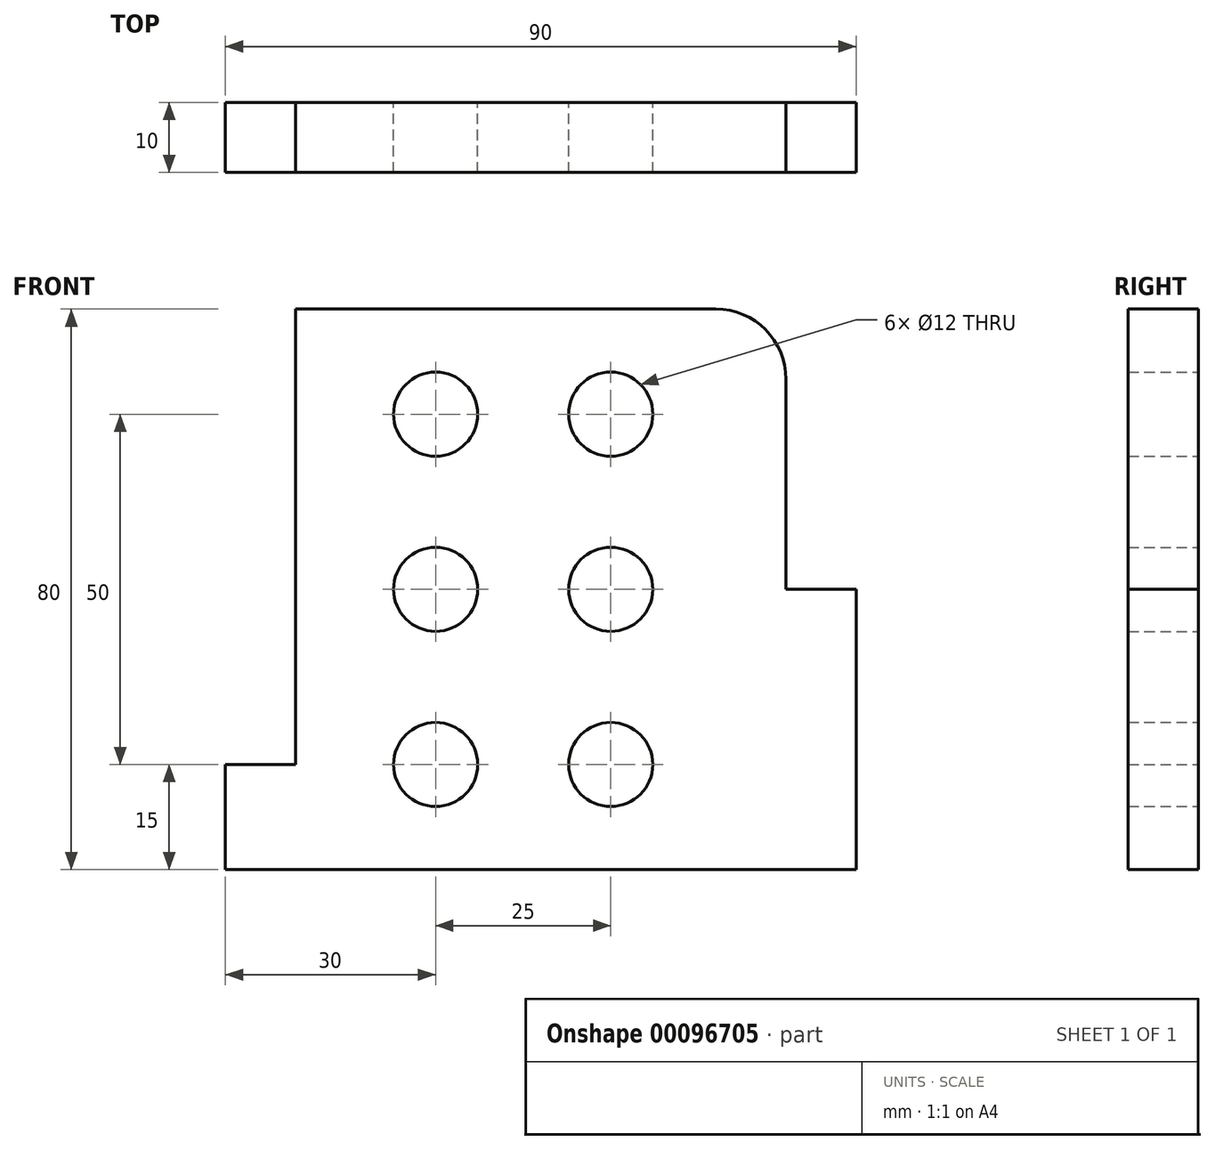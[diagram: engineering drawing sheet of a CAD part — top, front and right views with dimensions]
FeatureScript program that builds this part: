
annotation { "Feature Type Name" : "Feature", "Feature Type Description" : "" }
export const myFeature = defineFeature(function(context is Context, id is Id, definition is map)
    precondition{}
    {
        {
            var Q0;
            Q0=qCreatedBy(makeId("Front.planeOp"),FACE);
            var sketch = newSketch(context, id + "F0", { "sketchPlane" : qUnion([Q0])});
            skLineSegment(sketch, "E0", {"start": v(0, 0) * mm, "end": v(0, 15) * mm});
            skLineSegment(sketch, "E1", {"start": v(10, 15) * mm, "end": v(10, 80) * mm});
            skLineSegment(sketch, "E2", {"start": v(10, 80) * mm, "end": v(70, 80) * mm});
            skLineSegment(sketch, "E3", {"start": v(0, 0) * mm, "end": v(90, 0) * mm});
            skLineSegment(sketch, "E4", {"start": v(90, 0) * mm, "end": v(90, 40) * mm});
            skLineSegment(sketch, "E5", {"start": v(90, 40) * mm, "end": v(80, 40) * mm});
            skLineSegment(sketch, "E6", {"start": v(80, 40) * mm, "end": v(80, 70) * mm});
            skArc(sketch, "E7", {"start": v(80, 70) * mm, "mid": v(77.07, 77.07) * mm, "end": v(70, 80) * mm});
            skCircle(sketch, "E8", {"center": v(30, 15) * mm, "radius": 6 * mm});
            skCircle(sketch, "E9", {"center": v(55, 15) * mm, "radius": 6 * mm});
            skCircle(sketch, "E10", {"center": v(55, 40) * mm, "radius": 6 * mm});
            skCircle(sketch, "E11", {"center": v(30, 40) * mm, "radius": 6 * mm});
            skCircle(sketch, "E12", {"center": v(30, 65) * mm, "radius": 6 * mm});
            skCircle(sketch, "E13", {"center": v(55, 65) * mm, "radius": 6 * mm});
            skLineSegment(sketch, "E14", {"start": v(10, 15) * mm, "end": v(0, 15) * mm});
            skSolve(sketch);
        }
        {
            var Q0;
            Q0 = qSketchRegion(id + "F0", true);
            extrude(context, id + "F1", {"entities" : qUnion([Q0]), "depth" : 10 * mm});
        }
    });
